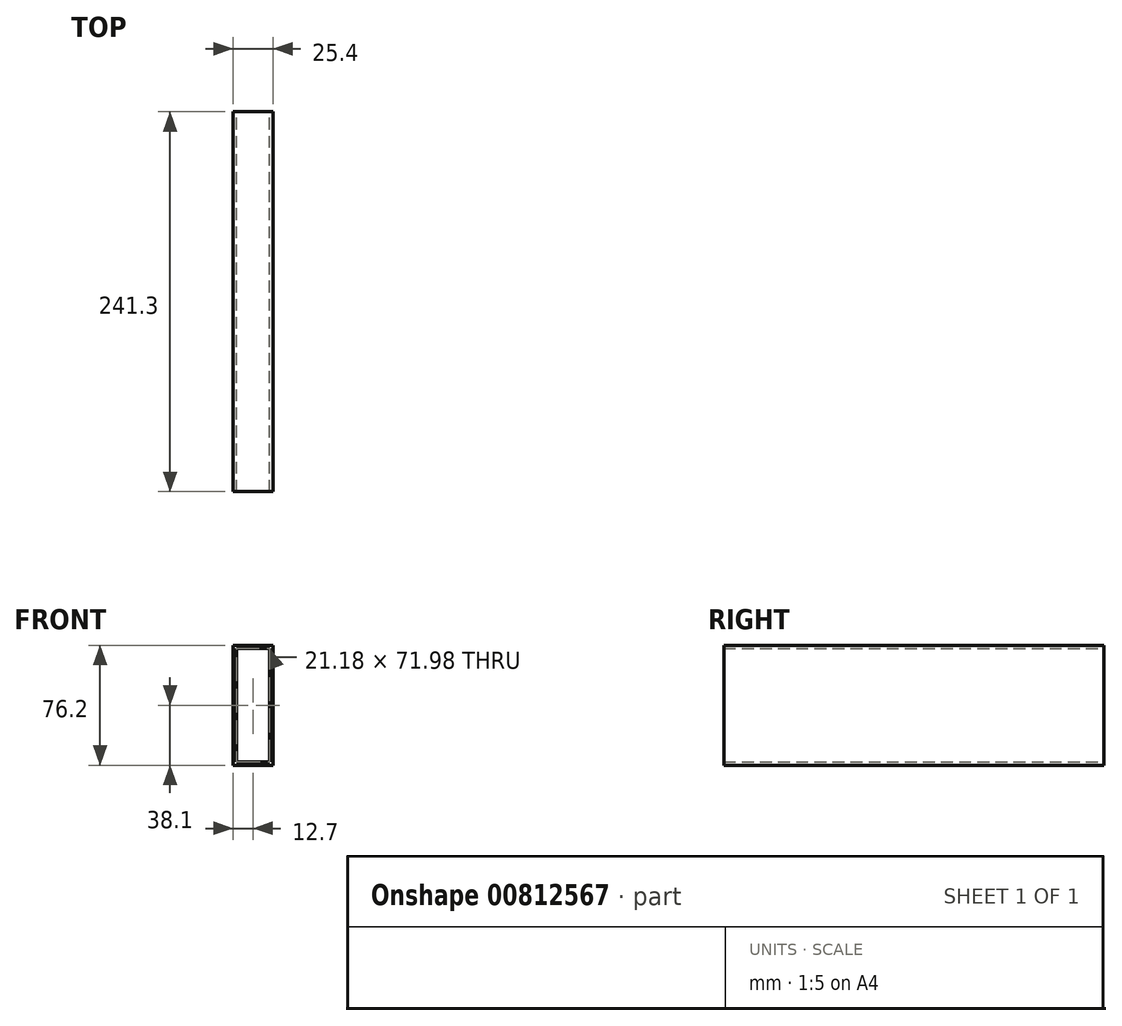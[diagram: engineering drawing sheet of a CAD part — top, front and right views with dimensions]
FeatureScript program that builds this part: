
annotation { "Feature Type Name" : "Feature", "Feature Type Description" : "" }
export const myFeature = defineFeature(function(context is Context, id is Id, definition is map)
    precondition{}
    {
        {
            var Q0;
            Q0=qCreatedBy(makeId("Front.planeOp"),FACE);
            var sketch = newSketch(context, id + "F0", { "sketchPlane" : qUnion([Q0])});
            skLineSegment(sketch, "E0.bottom", {"start": v(12.7, 38.1) * mm, "end": v(-12.7, 38.1) * mm});
            skLineSegment(sketch, "E0.top", {"start": v(12.7, -38.1) * mm, "end": v(-12.7, -38.1) * mm});
            skLineSegment(sketch, "E0.left", {"start": v(12.7, 38.1) * mm, "end": v(12.7, -38.1) * mm});
            skLineSegment(sketch, "E0.right", {"start": v(-12.7, 38.1) * mm, "end": v(-12.7, -38.1) * mm});
            skPoint(sketch, "E0.middle", {"position": v(0, 0) * mm});
            skLineSegment(sketch, "E1.0", {"start": v(10.6, 36) * mm, "end": v(-10.6, 36) * mm});
            skLineSegment(sketch, "E1.1", {"start": v(10.6, 36) * mm, "end": v(10.6, -36) * mm});
            skLineSegment(sketch, "E1.2", {"start": v(10.6, -36) * mm, "end": v(-10.6, -36) * mm});
            skLineSegment(sketch, "E1.3", {"start": v(-10.6, 36) * mm, "end": v(-10.6, -36) * mm});
            skSolve(sketch);
        }
        {
            var Q0;
            Q0=makeQuery(id+"F0.imprint","IMPRINT",FACE,{"disambiguationData":[TD([[makeQuery(id+"F0.imprint","IMPRINT",EDGE,{"derivedFrom":sQuery(id+"F0.wireOp",EDGE,"E0.bottom")}),1.0]])]});
            extrude(context, id + "F1", {"entities" : qUnion([Q0]), "endBound" : BoundingType.SYMMETRIC, "depth" : 241.3 * mm, "offsetDistance" : 25.4 * mm});
        }
    });
